# Revit family: ed
name_source: partatom
category: Generic Models
revit_build: Autodesk Revit 2018 (Build: 20190510_1515(x64)
units: mm (PartAtom-declared; Revit-internal decimal feet)

## family parameters
Can host rebar = No
Cut with Voids When Loaded = No
Host = Face
OmniClass Number = 23.31.17.00
OmniClass Title = Showers
Part Type = Normal
Room Calculation Point = No
Round Connector Dimension = Use Diameter
Shared = No

## types (2) — shared parameters
BIMobject category = Showers
Default Elevation = 1219 mm
Design country = Germany
ETIM classification = EC010132 | Hand shower holder
Edition number = 1
IFC Classification = Sanitary Terminal
Installation instructions = https://pro.duravit.com
Manufacturer = Duravit
Manufacturer country = Germany
Manufacturer name = DURAVIT AG
Masterformat 2014 Code = 22 41 23
Masterformat 2014 Description = Residential Showers
Material main = Brass
Model = Hand shower holder 38x58x38 mm - UV0620001
OmniClass Code = 23-31 17 00
OmniClass Description = Showers
Product Guid = 08ead720-a5af-4f82-bde5-c8f1b68c6c1e
Product SKU = Hand-shower-holder-38x58x38-mm-UV0620001
Product certification = https://pro.duravit.com
Product data url = https://bimobject.com
Product family = Universal
Product group = Hand shower holder
Product name = Hand shower holder 38x58x38 mm - UV0620001
Product url = https://pro.duravit.com
QR code = https://bimobject.com
Technical description = https://pro.duravit.com
UNSPSC Code = 30181503
URL = https://www.duravit.com
Uniclass 2015 Code = SL_35_80_80
Uniclass 2015 Name = Showers
Uniformat II Code = D2010
Uniformat II Description = Plumbing Fixtures
Weight Net (Kg) = 0.032
Youtube clip = https://pro.duravit.com

## per-type parameters (varying)
| type | Description | Main material |
| 10 - Chrome | Duravit Hand shower holder Chrome High Gloss 38x58x38 mm - UV0620001010 | Duravit - Metal - 10 - Chrome |
| 46 - Black Matt | Duravit Hand shower holder Black Matt 38x58x38 mm - UV0620001046 | Duravit - Metal - 46 - Black Matt |

## geometry (parser evidence)
native form markers: Sweep x4
no freeform markers — native parametric forms only
